# Revit family: 94532022
name_source: partatom
category: Modelos genéricos
revit_build: Autodesk Revit 2016 (Build: 20150220_1215(x64)
units: mm (PartAtom-declared; Revit-internal decimal feet)

## family parameters
Com base no plano de trabalho = Não
Compartilhado = Não
Corte com vazios quando carregados = Não
Cota do conector redondo = Utilizar diâmetro
Pode hospedar o vergalhão = Não
Ponto de cálculo do ambiente = Não
Sempre na vertical = Sim
Tipo de parte = Normal

## types (1)
- Bandeja p Cuba - 94532022
    Acabamento = Scotch brite
    Bordas = apoios em silicone
    Comentários de tipos = Compativel com as seguintes referências das linhas Vitrum e Quadrum: 94004 / 94005 / 94006 /94007 /94008/ 93915/93917/ 93918/ 93920 / 93954 / 93955 / 93956 / 93957 / 93958
    Código de montagem = Bandeja p Cuba - 94532022
    Descrição = Tramontina - Lixeira com pedal - 94538130
    Desenvolvedor = Factory Cursos & Desenvolvimento
    Espessura = 1 mm
    Fabricante = Tramontina
    Referencia = Bandeja p Cuba - 94532022
    Site do desenvolvedor = www.factorycursos.com.br
    Tipo de imagem = <Nenhum>
    URL = www.tramontina.com.br
